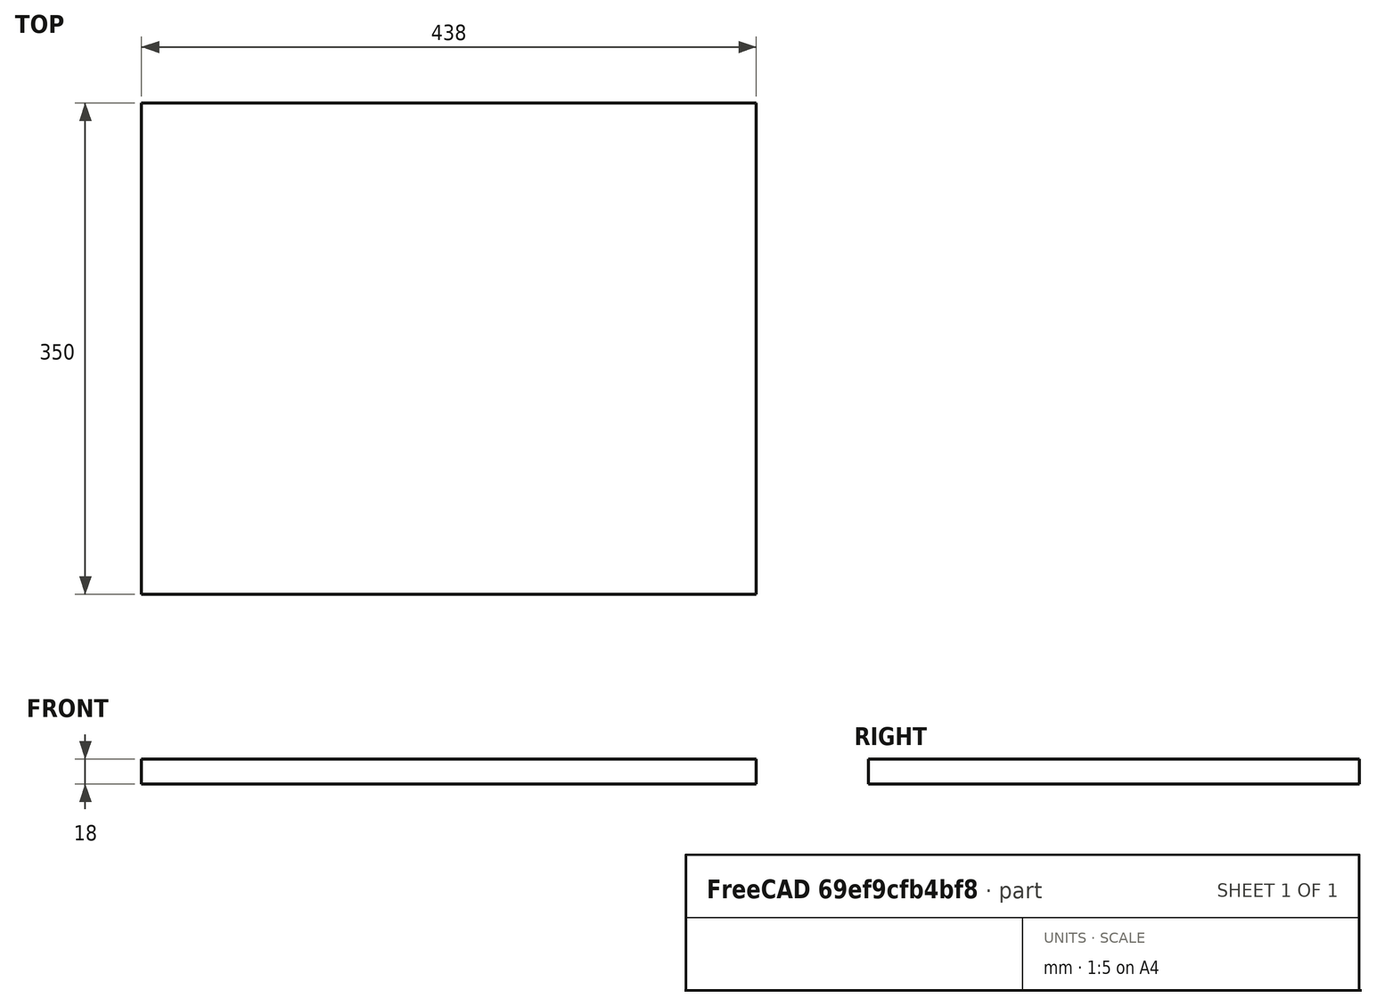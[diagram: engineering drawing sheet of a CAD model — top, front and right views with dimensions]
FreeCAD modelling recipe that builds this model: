
FCSTD DOCUMENT  (FreeCAD 0.18R4 (GitTag))
Label: drawer_bottom
License: All rights reserved
LicenseURL: http://en.wikipedia.org/wiki/All_rights_reserved
objects: Sketcher::SketchObject×1, PartDesign::Pad×1, PartDesign::Body×1
note: 4 computed .brp shape members not serialized (recipe doc carries the construction recipe); baked Part::Feature solids carry a one-line shape summary decoded from their .brp

FEATURE [Sketcher::SketchObject] Sketch
  MapMode = 5
  Support = -> [XY_Plane]
  sketch-geometry (4):
    g0: LineSegment StartX=0 StartY=0 StartZ=0 EndX=-438 EndY=0 EndZ=0
    g1: LineSegment StartX=-438 StartY=0 StartZ=0 EndX=-438 EndY=350 EndZ=0
    g2: LineSegment StartX=-438 StartY=350 StartZ=0 EndX=0 EndY=350 EndZ=0
    g3: LineSegment StartX=0 StartY=350 StartZ=0 EndX=0 EndY=0 EndZ=0
  constraints (11):
    c: Coincident(g0,g1)
    c: Coincident(g1,g2)
    c: Coincident(g2,g3)
    c: Coincident(g3,g0)
    c: Horizontal(g0)
    c: Horizontal(g2)
    c: Vertical(g1)
    c: Vertical(g3)
    c: Coincident(g0,g-1)
    c: DistanceX(g0,g0) = 438
    c: DistanceY(g3,g3) = 350
FEATURE [PartDesign::Pad] Pad
  Length = 18
  Length2 = 100
  Profile = -> Sketch
  Type = 0
FEATURE [PartDesign::Body] Body
  Group = -> [Sketch,Pad]
  Origin = -> Origin
  Tip = -> Pad
